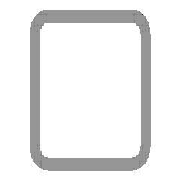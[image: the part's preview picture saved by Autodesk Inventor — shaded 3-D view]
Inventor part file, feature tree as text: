
AUTODESK INVENTOR PART (.ipt)
format: ipt  version: 2025 (Build 290162010, 162A)  size: 134,144 bytes
history: native  units: mm (DEFAULTED — no unit token found)
features: other x4, sketch x1, plane x1
ambient origin geometry x8: Origin, YZ Plane, XZ Plane, XY Plane, X Axis, Y Axis, Z Axis, Center Point
bodies: Solid1 (feature_tree), Body (feature_tree)
feature tree (6):
  parser-record x1  (decoder bookkeeping rows leaked as tree rows — omitted from the tree; the rows remain in map.json)
  other  "Driven Length"
  other  "Start Plane"
  other  "End Plane"
  sketch  "Sketch3"  dims[d3=1050.0mm d4=0.0mm d7=8.0mm d9=100.0mm d11=100.0mm d12=4.0mm d13=50.0mm d14=1100.0mm d15=50.0mm d16=50.0mm d17=90.0deg d18=1050.0mm]
  plane  "Work Plane3"
